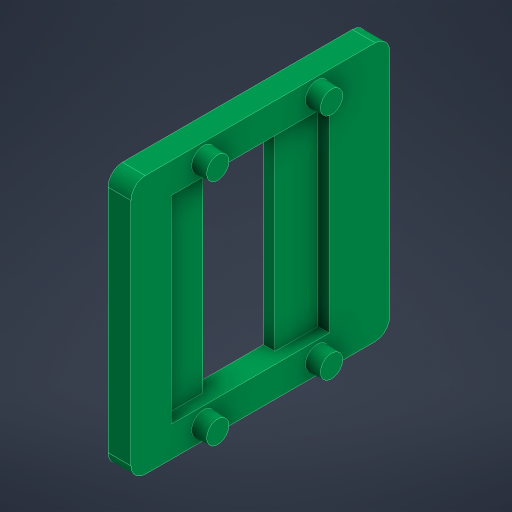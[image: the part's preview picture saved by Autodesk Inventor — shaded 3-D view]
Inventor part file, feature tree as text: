
AUTODESK INVENTOR PART (.ipt)
format: ipt  version: 2023.4 (Build 274418000, 418)  size: 254,464 bytes
history: native  units: mm
features: chamfer x4, other x4, extrude x3, sketch x3, reference x3, plane x2, projected_geometry x1
ambient origin geometry x8: Origin, YZ Plane, XZ Plane, XY Plane, X Axis, Y Axis, Z Axis, Center Point
bodies: Solid1 (feature_tree)
feature tree (20):
  plane  "Work Plane1"
  extrude  "Extrusion1"  Depth=45.0mm
  sketch  "Sketch2"  dims[d2=2.5mm d3=2.5mm]
  plane  "Work Plane2"
  extrude  "Extrusion2"  Depth=2.5mm
  chamfer  "Chamfer1"  Distance=4.0mm
  chamfer  "Chamfer2"  Distance=2.0mm
  chamfer  "Chamfer3"  Distance=2.5mm Angle=45.0deg
  chamfer  "Chamfer4"  Distance=2.5mm Angle=45.0deg
  extrude  "Extrusion3"  Depth=2.5mm TaperAngle=45.0deg
  sketch  "Sketch1"  dims[d0=45.0mm d1=45.0mm]
  reference  "Reference1"
  reference  "Reference2"
  reference  "Reference3"
  sketch  "Sketch3"  dims[d4=34.5mm d5=4.0mm d6=0.0mm d7=2.0mm d8=0.0mm d9=0.125mm d10=2.5mm d11=45.0deg d12=0.125mm d13=2.5mm d14=45.0deg d15=0.125mm d16=2.5mm d17=45.0deg d18=0.125mm d19=2.5mm d20=45.0deg d21=7.5mm d22=7.5mm d23=2.0mm d24=0.0mm]
  projected_geometry  "Projected Loop1"
  other  "<path>\Projects\Project Protocube\Protocube\CAD, STL, OBJ Files\1 CAD\Cube 1x1 V5.iam"
  other  "Cube 1x1 V5.iam"
  other  "Cube 1x1 Bottom V5 Closed Slotted:1"
  other  "Cube 1x1 Top V5 Closed Slotted:1"
note: 1 file-system path scrubbed to <path> (originals preserved in map.json)
